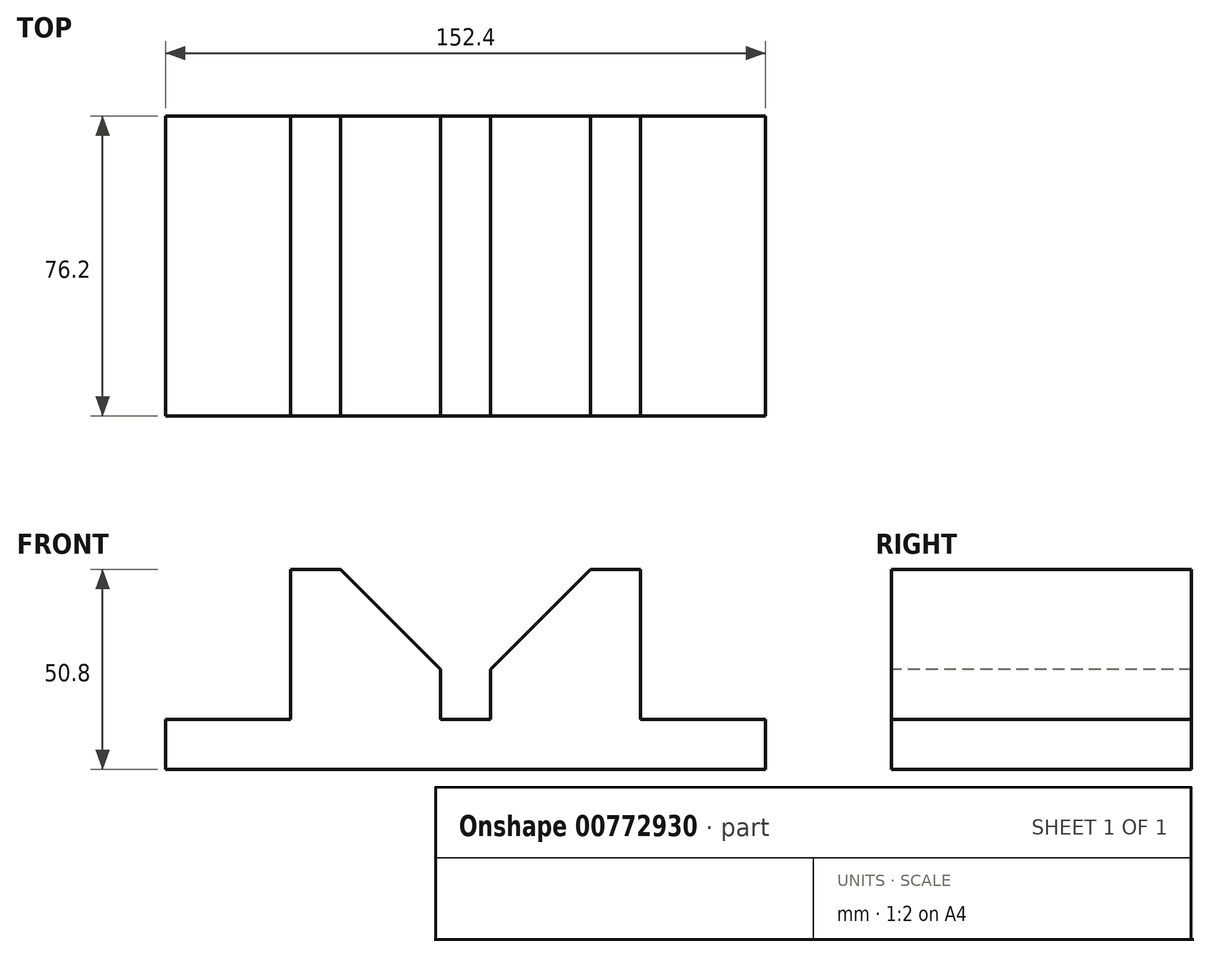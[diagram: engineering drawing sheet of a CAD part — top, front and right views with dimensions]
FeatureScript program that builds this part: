
annotation { "Feature Type Name" : "Feature", "Feature Type Description" : "" }
export const myFeature = defineFeature(function(context is Context, id is Id, definition is map)
    precondition{}
    {
        {
            var Q0;
            Q0=qCreatedBy(makeId("Front.planeOp"),FACE);
            var sketch = newSketch(context, id + "F0", { "sketchPlane" : qUnion([Q0])});
            skLineSegment(sketch, "E0", {"start": v(0, 0) * mm, "end": v(152.4, 0) * mm});
            skLineSegment(sketch, "E1", {"start": v(152.4, 0) * mm, "end": v(152.4, 50.8) * mm});
            skLineSegment(sketch, "E2", {"start": v(152.4, 50.8) * mm, "end": v(0, 50.8) * mm});
            skLineSegment(sketch, "E3", {"start": v(0, 50.8) * mm, "end": v(0, 0) * mm});
            skSolve(sketch);
        }
        {
            var Q0;
            Q0=makeQuery(id+"F0.imprint","IMPRINT",FACE,{"disambiguationData":[TD([[makeQuery(id+"F0.imprint","IMPRINT",EDGE,{"derivedFrom":sQuery(id+"F0.wireOp",EDGE,"E0")}),1.0]])]});
            extrude(context, id + "F1", {"entities" : qUnion([Q0]), "depth" : 76.2 * mm, "offsetDistance" : 25.4 * mm});
        }
        {
            var Q0;
            Q0=makeQuery(id+"F1.opExtrude","SWEPT_FACE",FACE,{"disambiguationData":[OSD([sQuery(id+"F0.wireOp",EDGE,"E2")])]});
            var sketch = newSketch(context, id + "F2", { "sketchPlane" : qUnion([Q0])});
            skLineSegment(sketch, "E4", {"start": v(152.4, 0) * mm, "end": v(120.65, 0) * mm});
            skLineSegment(sketch, "E5", {"start": v(120.65, 0) * mm, "end": v(120.65, -76.2) * mm});
            skSolve(sketch);
        }
        {
            var Q0;
            Q0=makeQuery(id+"F2.imprint","IMPRINT",FACE,{"disambiguationData":[TD([[makeQuery(id+"F2.imprint","IMPRINT",EDGE,{"derivedFrom":sQuery(id+"F2.wireOp",EDGE,"E4")}),1.0]])]});
            extrude(context, id + "F3", {"entities" : qUnion([Q0]), "operationType" : NewBodyOperationType.REMOVE, "oppositeDirection" : true, "depth" : 38.1 * mm, "offsetDistance" : 25.4 * mm});
        }
        {
            var Q0;
            Q0=makeQuery(id+"F1.opExtrude","SWEPT_FACE",FACE,{"disambiguationData":[OSD([sQuery(id+"F0.wireOp",EDGE,"E2")])]});
            var sketch = newSketch(context, id + "F4", { "sketchPlane" : qUnion([Q0])});
            skLineSegment(sketch, "E6", {"start": v(0, 0) * mm, "end": v(31.75, 0) * mm});
            skLineSegment(sketch, "E7", {"start": v(31.75, 0) * mm, "end": v(31.75, -76.2) * mm});
            skSolve(sketch);
        }
        {
            var Q0;
            Q0=makeQuery(id+"F4.imprint","IMPRINT",FACE,{"disambiguationData":[TD([[makeQuery(id+"F4.imprint","IMPRINT",EDGE,{"derivedFrom":sQuery(id+"F4.wireOp",EDGE,"E6")}),1.0]])]});
            extrude(context, id + "F5", {"entities" : qUnion([Q0]), "operationType" : NewBodyOperationType.REMOVE, "oppositeDirection" : true, "depth" : 38.1 * mm, "offsetDistance" : 25.4 * mm});
        }
        {
            var Q0;
            Q0=makeQuery(id+"F1.opExtrude","CAP_FACE",FACE,{"disambiguationData":[OSD([sQuery(id+"F0.wireOp",EDGE,"E0"),sQuery(id+"F0.wireOp",EDGE,"E1"),sQuery(id+"F0.wireOp",EDGE,"E2"),sQuery(id+"F0.wireOp",EDGE,"E3")])],"isStart":false});
            var sketch = newSketch(context, id + "F6", { "sketchPlane" : qUnion([Q0])});
            skLineSegment(sketch, "E8", {"start": v(31.75, 50.8) * mm, "end": v(44.45, 50.8) * mm});
            skLineSegment(sketch, "E9", {"start": v(120.65, 50.8) * mm, "end": v(107.95, 50.8) * mm});
            skLineSegment(sketch, "E10", {"start": v(76.2, 0) * mm, "end": v(76.2, 25.4) * mm});
            skLineSegment(sketch, "E11", {"start": v(76.2, 25.4) * mm, "end": v(69.85, 25.4) * mm});
            skLineSegment(sketch, "E12", {"start": v(76.2, 25.4) * mm, "end": v(82.55, 25.4) * mm});
            skLineSegment(sketch, "E13", {"start": v(82.55, 25.4) * mm, "end": v(107.95, 50.8) * mm});
            skLineSegment(sketch, "E14", {"start": v(44.45, 50.8) * mm, "end": v(69.85, 25.4) * mm});
            skSolve(sketch);
        }
        {
            var Q0;
            Q0=makeQuery(id+"F6.imprint","IMPRINT",FACE,{"disambiguationData":[TD([[makeQuery(id+"F6.imprint","IMPRINT",EDGE,{"derivedFrom":sQuery(id+"F6.wireOp",EDGE,"E11")}),-1.0]])]});
            extrude(context, id + "F7", {"entities" : qUnion([Q0]), "operationType" : NewBodyOperationType.REMOVE, "oppositeDirection" : true, "depth" : 76.2 * mm, "offsetDistance" : 25.4 * mm});
        }
        {
            var Q0;
            Q0=makeQuery(id+"F1.opExtrude","CAP_FACE",FACE,{"disambiguationData":[OSD([sQuery(id+"F0.wireOp",EDGE,"E0"),sQuery(id+"F0.wireOp",EDGE,"E1"),sQuery(id+"F0.wireOp",EDGE,"E2"),sQuery(id+"F0.wireOp",EDGE,"E3")])],"isStart":false});
            var sketch = newSketch(context, id + "F8", { "sketchPlane" : qUnion([Q0])});
            skLineSegment(sketch, "E15", {"start": v(69.85, 25.4) * mm, "end": v(69.85, 12.7) * mm});
            skLineSegment(sketch, "E16", {"start": v(69.85, 12.7) * mm, "end": v(82.55, 12.7) * mm});
            skLineSegment(sketch, "E17", {"start": v(82.55, 12.7) * mm, "end": v(82.55, 25.4) * mm});
            skSolve(sketch);
        }
        {
            var Q0;
            Q0=makeQuery(id+"F8.imprint","IMPRINT",FACE,{"disambiguationData":[TD([[makeQuery(id+"F8.imprint","IMPRINT",EDGE,{"derivedFrom":sQuery(id+"F8.wireOp",EDGE,"E15")}),1.0]])]});
            extrude(context, id + "F9", {"entities" : qUnion([Q0]), "operationType" : NewBodyOperationType.REMOVE, "oppositeDirection" : true, "depth" : 76.2 * mm, "offsetDistance" : 25.4 * mm});
        }
    });
